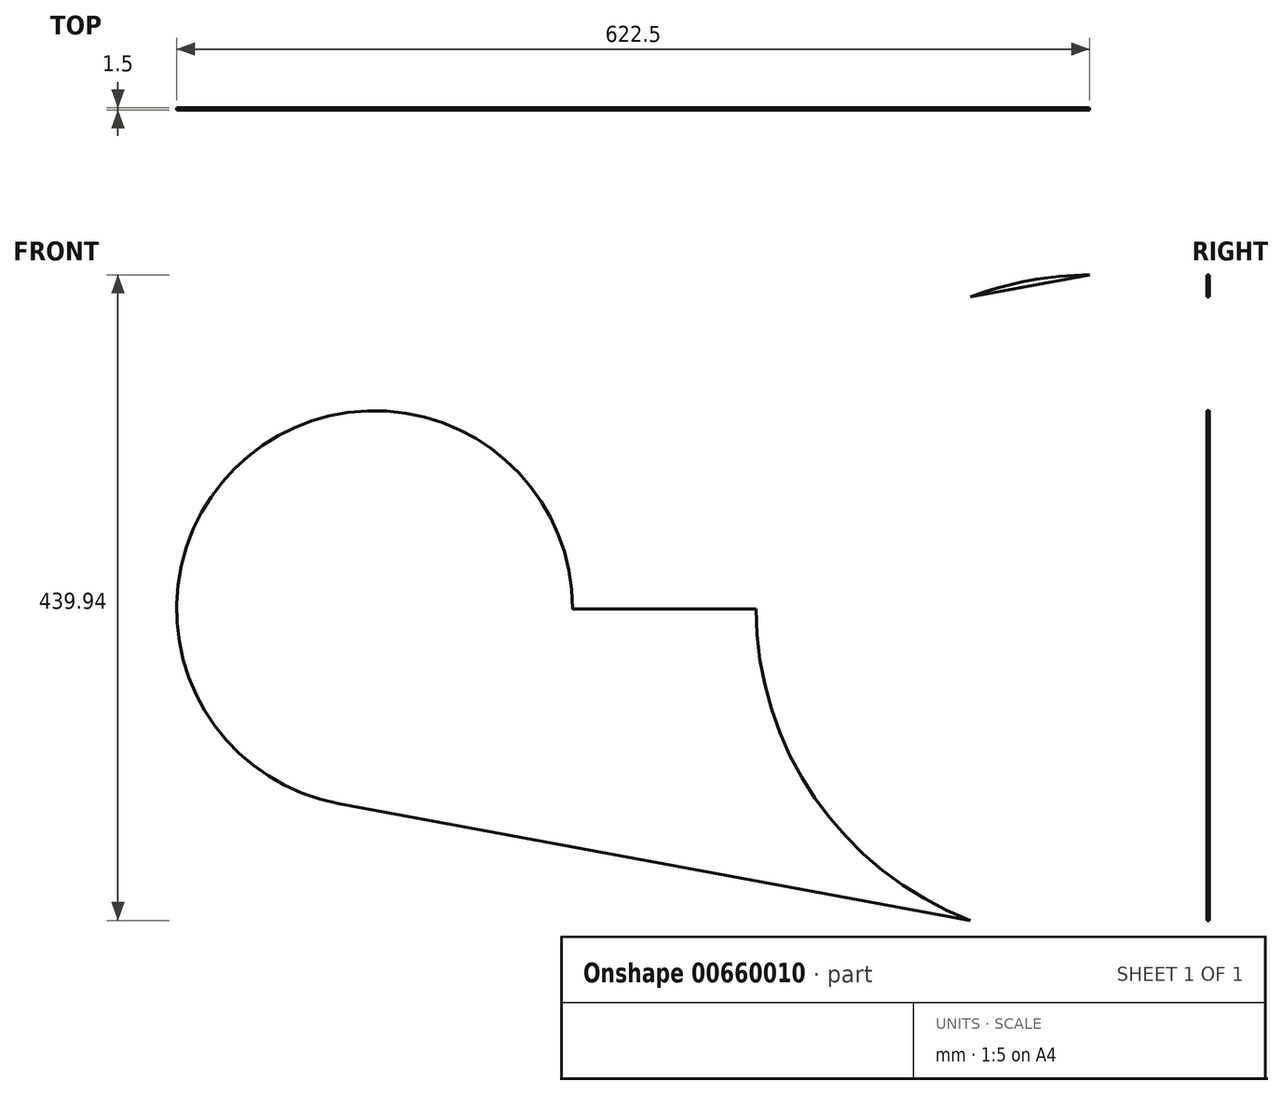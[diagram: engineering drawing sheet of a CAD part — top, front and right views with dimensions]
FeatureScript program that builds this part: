
annotation { "Feature Type Name" : "Feature", "Feature Type Description" : "" }
export const myFeature = defineFeature(function(context is Context, id is Id, definition is map)
    precondition{}
    {
        {
            var Q0;
            Q0=qCreatedBy(makeId("Front.planeOp"),FACE);
            var sketch = newSketch(context, id + "F0", { "sketchPlane" : qUnion([Q0])});
            skCircle(sketch, "E0", {"center": v(0, 0) * mm, "radius": 227.5 * mm});
            skCircle(sketch, "E1", {"center": v(-487.5, 0) * mm, "radius": 135 * mm});
            skLineSegment(sketch, "E2", {"start": v(0, 0) * mm, "end": v(-910.58, 0) * mm});
            skLineSegment(sketch, "E3", {"start": v(0, 227.5) * mm, "end": v(-512.06, 132.75) * mm});
            skLineSegment(sketch, "E4", {"start": v(0, -227.5) * mm, "end": v(-512.06, -132.75) * mm});
            skSolve(sketch);
        }
        {
            var Q0;
            {var subQ0=sQuery(id+"F0.wireOp",EDGE,"E2");var subQ1=sQuery(id+"F0.wireOp",EDGE,"E0");var subQ2=makeQuery(id+"F0.imprint","INTERSECT",VERTEX,{"derivedFrom":[subQ1,subQ0]});Q0=makeQuery(id+"F0.imprint","IMPRINT",FACE,{"disambiguationData":[TD([[makeQuery(id+"F0.imprint","IMPRINT",EDGE,{"disambiguationData":[TD([[subQ2,-1.0]])],"derivedFrom":subQ1}),-1.0]])]});}
            var Q1;
            {var subQ0=sQuery(id+"F0.wireOp",EDGE,"E3");var subQ1=sQuery(id+"F0.wireOp",EDGE,"E0");var subQ7=makeQuery(id+"F0.imprint","INTERSECT",VERTEX,{"disambiguationData":[OD(1.0)],"derivedFrom":[subQ1,subQ0]});Q1=makeQuery(id+"F0.imprint","IMPRINT",FACE,{"disambiguationData":[TD([[makeQuery(id+"F0.imprint","IMPRINT",EDGE,{"disambiguationData":[TD([[subQ7,-1.0]])],"derivedFrom":subQ1}),1.0]])]});}
            var Q2;
            {var subQ0=sQuery(id+"F0.wireOp",EDGE,"E3");var subQ1=sQuery(id+"F0.wireOp",EDGE,"E0");var subQ2=makeQuery(id+"F0.imprint","INTERSECT",VERTEX,{"disambiguationData":[OD(1.0)],"derivedFrom":[subQ1,subQ0]});Q2=makeQuery(id+"F0.imprint","IMPRINT",FACE,{"disambiguationData":[TD([[makeQuery(id+"F0.imprint","IMPRINT",EDGE,{"disambiguationData":[TD([[subQ2,-1.0]])],"derivedFrom":subQ1}),-1.0]])]});}
            var Q3;
            {var subQ0=sQuery(id+"F0.wireOp",EDGE,"E1");var subQ1=makeQuery(id+"F0.imprint","INTERSECT",VERTEX,{"derivedFrom":[subQ0,sQuery(id+"F0.wireOp",EDGE,"E4")]});Q3=makeQuery(id+"F0.imprint","IMPRINT",FACE,{"disambiguationData":[TD([[makeQuery(id+"F0.imprint","IMPRINT",EDGE,{"disambiguationData":[TD([[subQ1,1.0]])],"derivedFrom":subQ0}),1.0]])]});}
            var Q4;
            {var subQ0=sQuery(id+"F0.wireOp",EDGE,"E1");var subQ1=makeQuery(id+"F0.imprint","INTERSECT",VERTEX,{"derivedFrom":[subQ0,sQuery(id+"F0.wireOp",EDGE,"E3")]});Q4=makeQuery(id+"F0.imprint","IMPRINT",FACE,{"disambiguationData":[TD([[makeQuery(id+"F0.imprint","IMPRINT",EDGE,{"disambiguationData":[TD([[subQ1,1.0]])],"derivedFrom":subQ0}),1.0]])]});}
            extrude(context, id + "F1", {"entities" : qUnion([Q0, Q1, Q2, Q3, Q4]), "endBound" : BoundingType.SYMMETRIC, "depth" : 1.5 * mm, "offsetDistance" : 25 * mm});
        }
    });
